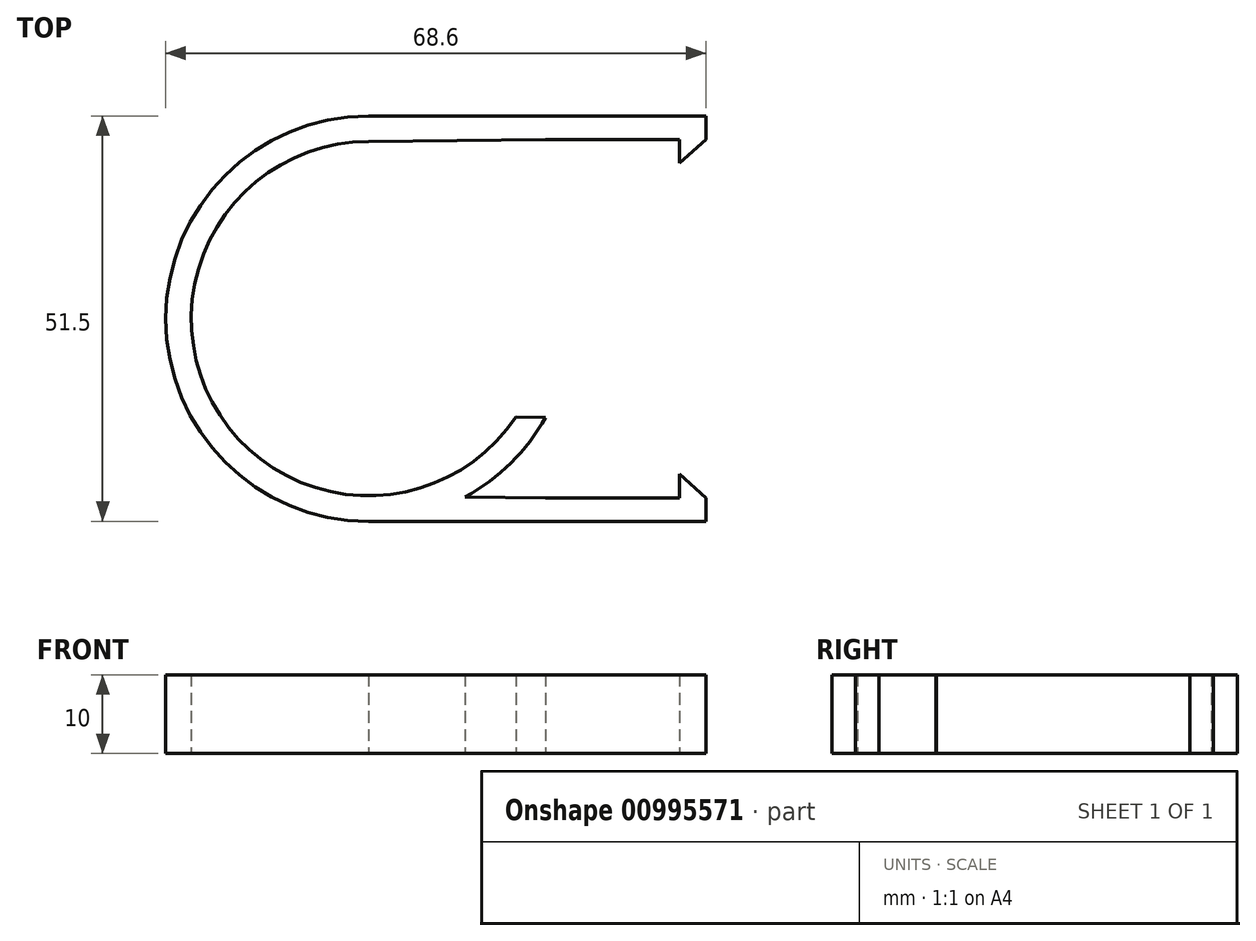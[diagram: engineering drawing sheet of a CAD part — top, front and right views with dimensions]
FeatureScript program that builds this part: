
annotation { "Feature Type Name" : "Feature", "Feature Type Description" : "" }
export const myFeature = defineFeature(function(context is Context, id is Id, definition is map)
    precondition{}
    {
        {
            var Q0;
            Q0=qCreatedBy(makeId("Top.planeOp"),FACE);
            var sketch = newSketch(context, id + "F0", { "sketchPlane" : qUnion([Q0])});
            skLineSegment(sketch, "E0", {"start": v(4.39, 23.32) * mm, "end": v(4.39, 20.32) * mm});
            skLineSegment(sketch, "E1", {"start": v(4.39, 20.32) * mm, "end": v(1.04, 17.32) * mm});
            skLineSegment(sketch, "E2", {"start": v(1.04, 17.32) * mm, "end": v(1.04, 20.32) * mm});
            skLineSegment(sketch, "E3", {"start": v(1.04, 20.32) * mm, "end": v(-15.96, 20.32) * mm});
            skLineSegment(sketch, "E4", {"start": v(-15.96, 20.32) * mm, "end": v(-15.96, -25.18) * mm, "construction": true});
            skPoint(sketch, "E5", {"position": v(-15.96, -2.43) * mm});
            skLineSegment(sketch, "E6", {"start": v(70.17, -2.43) * mm, "end": v(-91.58, -2.43) * mm, "construction": true});
            skLineSegment(sketch, "E7", {"start": v(-15.96, -2.43) * mm, "end": v(-38.46, -2.43) * mm, "construction": true});
            skCircle(sketch, "E8", {"center": v(-38.46, -2.43) * mm, "radius": 22.5 * mm, "construction": true});
            skLineSegment(sketch, "E9", {"start": v(-38.46, -2.43) * mm, "end": v(-38.46, 20.07) * mm, "construction": true});
            skLineSegment(sketch, "E10", {"start": v(-38.46, -2.43) * mm, "end": v(-38.46, -24.93) * mm, "construction": true});
            skLineSegment(sketch, "E11", {"start": v(-15.96, 20.32) * mm, "end": v(-38.46, 20.07) * mm});
            skLineSegment(sketch, "E12", {"start": v(4.39, 23.32) * mm, "end": v(-38.46, 23.32) * mm});
            skArc(sketch, "E13", {"start": v(-38.46, 23.32) * mm, "mid": v(-56.67, 15.77) * mm, "end": v(-64.21, -2.43) * mm});
            skArc(sketch, "E14", {"start": v(-38.46, 20.07) * mm, "mid": v(-54.37, 13.48) * mm, "end": v(-60.96, -2.43) * mm});
            skArc(sketch, "E15", {"start": v(-38.46, 23.32) * mm, "mid": v(-32.13, 22.53) * mm, "end": v(-26.2, 20.2) * mm, "construction": true});
            skArc(sketch, "E16", {"start": v(-26.2, 20.2) * mm, "mid": v(-20.36, 15.87) * mm, "end": v(-15.96, 10.09) * mm});
            skLineSegment(sketch, "E17", {"start": v(-15.96, 10.09) * mm, "end": v(-19.74, 10.05) * mm});
            skArc(sketch, "E18", {"start": v(-38.46, 20.07) * mm, "mid": v(-27.85, 17.4) * mm, "end": v(-19.74, 10.05) * mm});
            skArc(sketch, "E19.MirrorCS", {"start": v(-38.46, -28.18) * mm, "mid": v(-56.67, -20.64) * mm, "end": v(-64.21, -2.43) * mm});
            skArc(sketch, "E20.MirrorCS", {"start": v(-38.46, -24.93) * mm, "mid": v(-54.37, -18.34) * mm, "end": v(-60.96, -2.43) * mm});
            skArc(sketch, "E21.MirrorCS", {"start": v(-38.46, -24.93) * mm, "mid": v(-27.85, -22.27) * mm, "end": v(-19.74, -14.91) * mm});
            skLineSegment(sketch, "E22.MirrorCS", {"start": v(4.39, -28.18) * mm, "end": v(-38.46, -28.18) * mm});
            skArc(sketch, "E23.MirrorCS", {"start": v(-26.2, -25.07) * mm, "mid": v(-20.36, -20.74) * mm, "end": v(-15.96, -14.96) * mm});
            skLineSegment(sketch, "E24.MirrorCS", {"start": v(-15.96, -25.18) * mm, "end": v(-38.46, -24.93) * mm});
            skLineSegment(sketch, "E25.MirrorCS", {"start": v(-15.96, -14.96) * mm, "end": v(-19.74, -14.91) * mm});
            skLineSegment(sketch, "E26.MirrorCS", {"start": v(1.04, -25.18) * mm, "end": v(-15.96, -25.18) * mm});
            skLineSegment(sketch, "E27.MirrorCS", {"start": v(1.04, -22.18) * mm, "end": v(1.04, -25.18) * mm});
            skLineSegment(sketch, "E28.MirrorCS", {"start": v(4.39, -25.18) * mm, "end": v(1.04, -22.18) * mm});
            skLineSegment(sketch, "E29.MirrorCS", {"start": v(4.39, -28.18) * mm, "end": v(4.39, -25.18) * mm});
            skSolve(sketch);
        }
        {
            var Q0;
            Q0=makeQuery(id+"F0.imprint","IMPRINT",FACE,{"disambiguationData":[TD([[makeQuery(id+"F0.imprint","IMPRINT",EDGE,{"derivedFrom":sQuery(id+"F0.wireOp",EDGE,"E0")}),-1.0]])]});
            var Q1;
            {var subQ2=sQuery(id+"F0.wireOp",EDGE,"E16");Q1=makeQuery(id+"F0.imprint","IMPRINT",FACE,{"disambiguationData":[TD([[makeQuery(id+"F0.imprint","IMPRINT",EDGE,{"derivedFrom":subQ2}),-1.0]])]});}
            var Q2;
            {var subQ0=sQuery(id+"F0.wireOp",EDGE,"E21.MirrorCS");Q2=makeQuery(id+"F0.imprint","IMPRINT",FACE,{"disambiguationData":[TD([[makeQuery(id+"F0.imprint","IMPRINT",EDGE,{"derivedFrom":subQ0}),-1.0]])]});}
            extrude(context, id + "F1", {"entities" : qUnion([Q0, Q1, Q2]), "depth" : 10 * mm, "offsetDistance" : 25 * mm});
        }
    });
